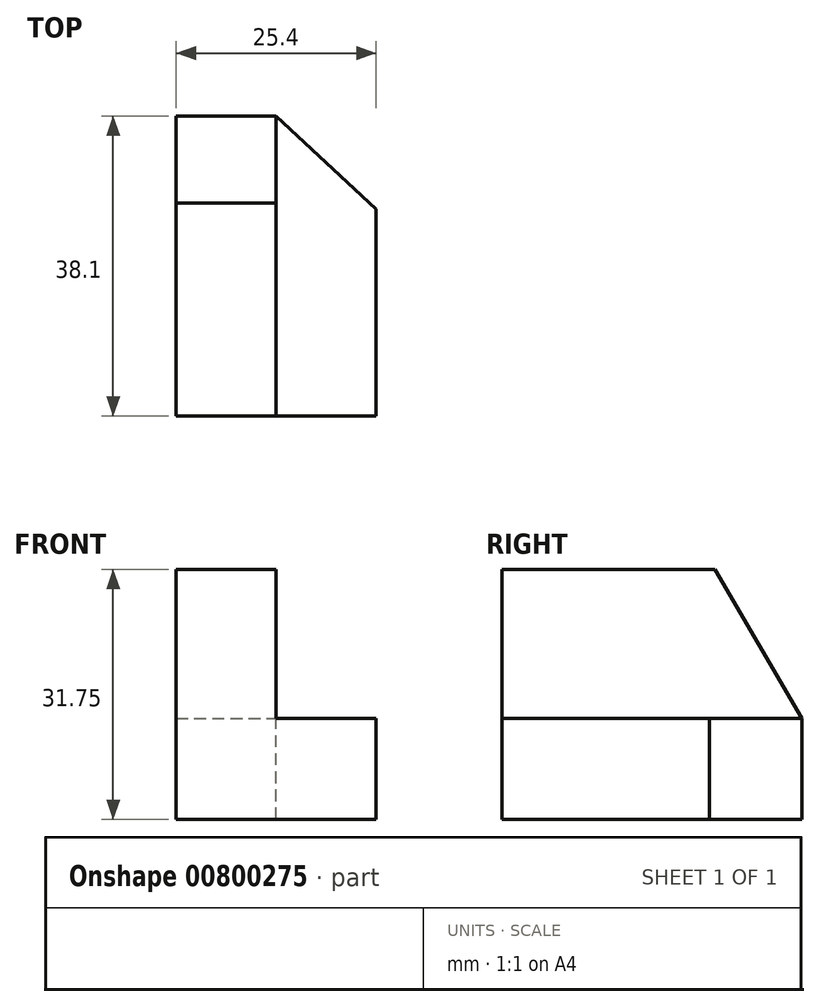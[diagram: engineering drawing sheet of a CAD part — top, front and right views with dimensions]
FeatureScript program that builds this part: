
annotation { "Feature Type Name" : "Feature", "Feature Type Description" : "" }
export const myFeature = defineFeature(function(context is Context, id is Id, definition is map)
    precondition{}
    {
        {
            var Q0;
            Q0=qCreatedBy(makeId("Right.planeOp"),FACE);
            var sketch = newSketch(context, id + "F0", { "sketchPlane" : qUnion([Q0])});
            skLineSegment(sketch, "E0", {"start": v(0, 0) * mm, "end": v(38.1, 0) * mm});
            skLineSegment(sketch, "E1", {"start": v(38.1, 0) * mm, "end": v(38.1, 31.75) * mm});
            skLineSegment(sketch, "E2", {"start": v(38.1, 31.75) * mm, "end": v(0, 31.75) * mm});
            skLineSegment(sketch, "E3", {"start": v(0, 31.75) * mm, "end": v(0, 0) * mm});
            skSolve(sketch);
        }
        {
            var Q0;
            Q0=makeQuery(id+"F0.imprint","IMPRINT",FACE,{"disambiguationData":[TD([[makeQuery(id+"F0.imprint","IMPRINT",EDGE,{"derivedFrom":sQuery(id+"F0.wireOp",EDGE,"E0")}),1.0]])]});
            extrude(context, id + "F1", {"entities" : qUnion([Q0]), "depth" : 25.4 * mm});
        }
        {
            var Q0;
            Q0=makeQuery(id+"F1.opExtrude","SWEPT_FACE",FACE,{"disambiguationData":[OSD([sQuery(id+"F0.wireOp",EDGE,"E2")])]});
            var sketch = newSketch(context, id + "F2", { "sketchPlane" : qUnion([Q0])});
            skLineSegment(sketch, "E4", {"start": v(12.7, 0) * mm, "end": v(12.7, 38.1) * mm});
            skSolve(sketch);
        }
        {
            var Q0;
            Q0=qSketchRegion(id+"F2",true);
            var Q1;
            {var subQ0=sQuery(id+"F2.wireOp",EDGE,"E4");Q1=makeQuery(id+"F2.imprint","IMPRINT",FACE,{"disambiguationData":[TD([[makeQuery(id+"F2.imprint","IMPRINT",EDGE,{"derivedFrom":subQ0}),-1.0]])]});}
            extrude(context, id + "F3", {"entities" : qUnion([Q0, Q1]), "operationType" : NewBodyOperationType.REMOVE, "oppositeDirection" : true, "depth" : 25.4 * mm});
        }
        {
            var Q0;
            Q0=makeQuery(id+"F3.boolean.opBoolean","COPY",FACE,{"derivedFrom":makeQuery(id+"F3.opExtrude","SWEPT_FACE",FACE,{"disambiguationData":[OSD([sQuery(id+"F2.wireOp",EDGE,"E4")])]})});
            var sketch = newSketch(context, id + "F4", { "sketchPlane" : qUnion([Q0])});
            skLineSegment(sketch, "E5", {"start": v(0, 12.84) * mm, "end": v(38.1, 12.84) * mm});
            skSolve(sketch);
        }
        {
            var Q0;
            Q0=qSketchRegion(id+"F4",true);
            var Q1;
            {var subQ0=sQuery(id+"F4.wireOp",EDGE,"E5");Q1=makeQuery(id+"F4.imprint","IMPRINT",FACE,{"disambiguationData":[TD([[makeQuery(id+"F4.imprint","IMPRINT",EDGE,{"derivedFrom":subQ0}),-1.0]])]});}
            extrude(context, id + "F5", {"entities" : qUnion([Q0, Q1]), "operationType" : NewBodyOperationType.ADD, "depth" : 12.7 * mm});
        }
        {
            var Q0;
            Q0=makeQuery(id+"F3.boolean.opBoolean","COPY",FACE,{"derivedFrom":makeQuery(id+"F3.opExtrude","SWEPT_FACE",FACE,{"disambiguationData":[OSD([sQuery(id+"F2.wireOp",EDGE,"E4")])]})});
            var sketch = newSketch(context, id + "F6", { "sketchPlane" : qUnion([Q0])});
            skLineSegment(sketch, "E6", {"start": v(38.1, 12.84) * mm, "end": v(27.02, 31.75) * mm});
            skSolve(sketch);
        }
        {
            var Q0;
            Q0=qSketchRegion(id+"F6",true);
            var Q1;
            {var subQ0=sQuery(id+"F6.wireOp",EDGE,"E6");Q1=makeQuery(id+"F6.imprint","IMPRINT",FACE,{"disambiguationData":[TD([[makeQuery(id+"F6.imprint","IMPRINT",EDGE,{"derivedFrom":subQ0}),-1.0]])]});}
            extrude(context, id + "F7", {"entities" : qUnion([Q0, Q1]), "operationType" : NewBodyOperationType.REMOVE, "oppositeDirection" : true, "depth" : 25.4 * mm});
        }
        {
            var Q0;
            Q0=makeQuery(id+"F5.opExtrude","SWEPT_FACE",FACE,{"disambiguationData":[OSD([sQuery(id+"F4.wireOp",EDGE,"E5")])]});
            var sketch = newSketch(context, id + "F8", { "sketchPlane" : qUnion([Q0])});
            skLineSegment(sketch, "E7", {"start": v(12.7, 38.1) * mm, "end": v(25.4, 26.3) * mm});
            skSolve(sketch);
        }
        {
            var Q0;
            Q0=qSketchRegion(id+"F8",true);
            var Q1;
            {var subQ0=sQuery(id+"F8.wireOp",EDGE,"E7");Q1=makeQuery(id+"F8.imprint","IMPRINT",FACE,{"disambiguationData":[TD([[makeQuery(id+"F8.imprint","IMPRINT",EDGE,{"derivedFrom":subQ0}),1.0]])]});}
            extrude(context, id + "F9", {"entities" : qUnion([Q0, Q1]), "operationType" : NewBodyOperationType.REMOVE, "oppositeDirection" : true, "depth" : 25.4 * mm});
        }
    });
